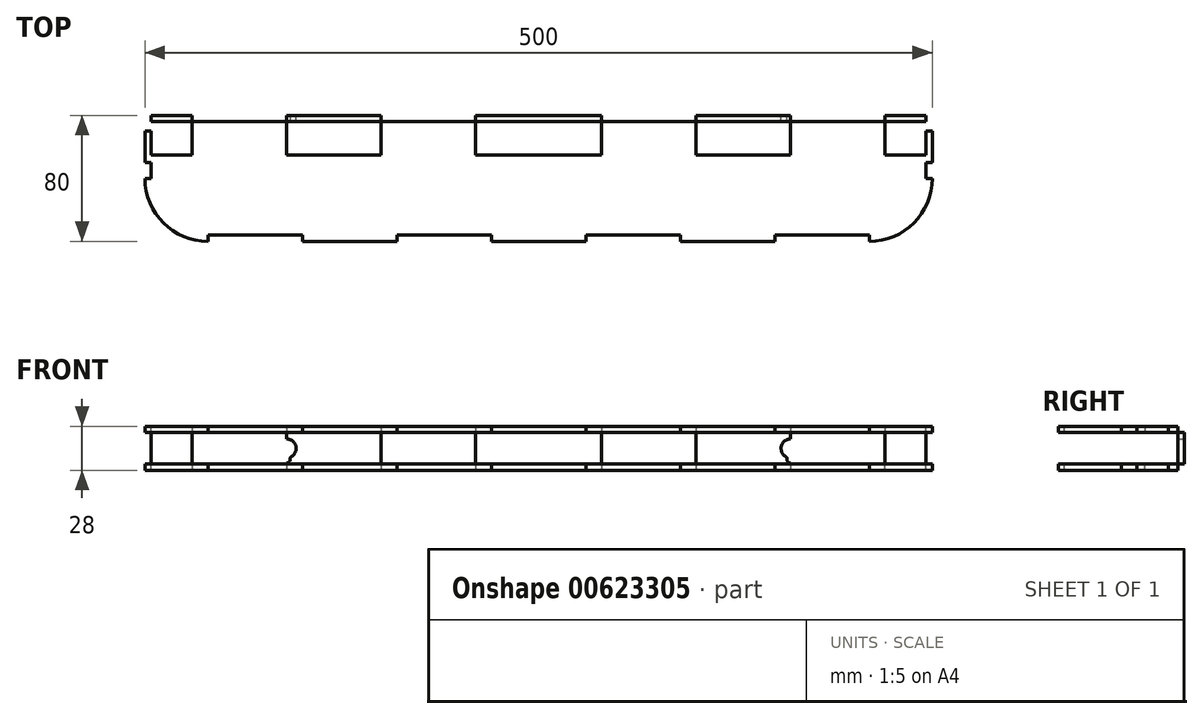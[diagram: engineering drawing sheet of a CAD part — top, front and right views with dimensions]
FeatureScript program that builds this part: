
annotation { "Feature Type Name" : "Feature", "Feature Type Description" : "" }
export const myFeature = defineFeature(function(context is Context, id is Id, definition is map)
    precondition{}
    {
        {
            var Q0;
            Q0=qCreatedBy(makeId("Top.planeOp"),FACE);
            var sketch = newSketch(context, id + "F0", { "sketchPlane" : qUnion([Q0])});
            skLineSegment(sketch, "E0.bottom", {"start": v(-250, 40) * mm, "end": v(250, 40) * mm});
            skLineSegment(sketch, "E0.top", {"start": v(-250, -40) * mm, "end": v(250, -40) * mm});
            skLineSegment(sketch, "E0.left", {"start": v(-250, 40) * mm, "end": v(-250, -40) * mm});
            skLineSegment(sketch, "E0.right", {"start": v(250, 40) * mm, "end": v(250, -40) * mm});
            skPoint(sketch, "E0.middle", {"position": v(0, 0) * mm});
            skSolve(sketch);
        }
        {
            var Q0;
            Q0=makeQuery(id+"F0.imprint","IMPRINT",FACE,{"disambiguationData":[TD([[makeQuery(id+"F0.imprint","IMPRINT",EDGE,{"derivedFrom":sQuery(id+"F0.wireOp",EDGE,"E0.bottom")}),-1.0]])]});
            extrude(context, id + "F1", {"entities" : qUnion([Q0]), "depth" : 4 * mm, "offsetDistance" : 25 * mm});
        }
        {
            var Q0;
            Q0=makeQuery(id+"F1.opExtrude","SWEPT_EDGE",EDGE,{"disambiguationData":[OSD([sQuery(id+"F0.wireOp",EDGE,"E0.top"),sQuery(id+"F0.wireOp",EDGE,"E0.left")])]});
            var Q1;
            Q1=makeQuery(id+"F1.opExtrude","SWEPT_EDGE",EDGE,{"disambiguationData":[OSD([sQuery(id+"F0.wireOp",EDGE,"E0.top"),sQuery(id+"F0.wireOp",EDGE,"E0.right")])]});
            fillet(context, id + "F2", {"entities" : qUnion([Q0, Q1]), "radius" : 40 * mm, "tangentPropagation" : true, "allowEdgeOverflow" : false});
        }
        {
            var Q0;
            Q0=makeQuery(id+"F1.opExtrude","CAP_FACE",FACE,{"disambiguationData":[OSD([sQuery(id+"F0.wireOp",EDGE,"E0.bottom"),sQuery(id+"F0.wireOp",EDGE,"E0.top"),sQuery(id+"F0.wireOp",EDGE,"E0.left"),sQuery(id+"F0.wireOp",EDGE,"E0.right")])],"isStart":true});
            cPlane(context, id + "F3", {"entities" : qUnion([Q0]), "cplaneType" : CPlaneType.OFFSET, "offset" : 10 * mm, "width" : 150 * mm, "height" : 150 * mm});
        }
        {
            var Q0;
            Q0=makeQuery(id+"F1.opExtrude","SWEPT_BODY",BODY,{"disambiguationData":[OSD([sQuery(id+"F0.wireOp",EDGE,"E0.bottom"),sQuery(id+"F0.wireOp",EDGE,"E0.top"),sQuery(id+"F0.wireOp",EDGE,"E0.left"),sQuery(id+"F0.wireOp",EDGE,"E0.right")])]});
            var Q1;
            Q1=qCreatedBy(id+"F3.planeOp",FACE);
            mirror(context, id + "F4", {"entities" : qUnion([Q0]), "mirrorPlane" : qUnion([Q1])});
        }
        {
            var Q0;
            Q0=makeQuery(id+"F1.opExtrude","SWEPT_FACE",FACE,{"disambiguationData":[OSD([sQuery(id+"F0.wireOp",EDGE,"E0.bottom")])]});
            var sketch = newSketch(context, id + "F5", { "sketchPlane" : qUnion([Q0])});
            skLineSegment(sketch, "E1.bottom", {"start": v(-250, 4) * mm, "end": v(250, 4) * mm});
            skLineSegment(sketch, "E1.top", {"start": v(-250, -24) * mm, "end": v(250, -24) * mm});
            skLineSegment(sketch, "E1.left", {"start": v(-250, 4) * mm, "end": v(-250, -24) * mm});
            skLineSegment(sketch, "E1.right", {"start": v(250, 4) * mm, "end": v(250, -24) * mm});
            skSolve(sketch);
        }
        {
            var Q0;
            Q0 = qSketchRegion(id + "F5", true);
            extrude(context, id + "F6", {"entities" : qUnion([Q0]), "oppositeDirection" : true, "depth" : 4 * mm, "offsetDistance" : 25 * mm});
        }
        {
            var Q0;
            Q0=makeQuery(id+"F1.opExtrude","CAP_FACE",FACE,{"disambiguationData":[OSD([sQuery(id+"F0.wireOp",EDGE,"E0.bottom"),sQuery(id+"F0.wireOp",EDGE,"E0.top"),sQuery(id+"F0.wireOp",EDGE,"E0.left"),sQuery(id+"F0.wireOp",EDGE,"E0.right")])],"isStart":false});
            var sketch = newSketch(context, id + "F7", { "sketchPlane" : qUnion([Q0])});
            skLineSegment(sketch, "E2.bottom", {"start": v(-210, -40) * mm, "end": v(-150, -40) * mm});
            skLineSegment(sketch, "E2.top", {"start": v(-210, -36) * mm, "end": v(-150, -36) * mm});
            skLineSegment(sketch, "E2.left", {"start": v(-210, -40) * mm, "end": v(-210, -36) * mm});
            skLineSegment(sketch, "E2.right", {"start": v(-150, -40) * mm, "end": v(-150, -36) * mm});
            skLineSegment(sketch, "E3.bottom", {"start": v(-90, -40) * mm, "end": v(-30, -40) * mm});
            skLineSegment(sketch, "E3.top", {"start": v(-90, -36) * mm, "end": v(-30, -36) * mm});
            skLineSegment(sketch, "E3.left", {"start": v(-90, -40) * mm, "end": v(-90, -36) * mm});
            skLineSegment(sketch, "E3.right", {"start": v(-30, -40) * mm, "end": v(-30, -36) * mm});
            skLineSegment(sketch, "E4.bottom", {"start": v(30, -40) * mm, "end": v(90, -40) * mm});
            skLineSegment(sketch, "E4.top", {"start": v(30, -36) * mm, "end": v(90, -36) * mm});
            skLineSegment(sketch, "E4.left", {"start": v(30, -40) * mm, "end": v(30, -36) * mm});
            skLineSegment(sketch, "E4.right", {"start": v(90, -40) * mm, "end": v(90, -36) * mm});
            skLineSegment(sketch, "E5.bottom", {"start": v(150, -40) * mm, "end": v(210, -40) * mm});
            skLineSegment(sketch, "E5.top", {"start": v(150, -36) * mm, "end": v(210, -36) * mm});
            skLineSegment(sketch, "E5.left", {"start": v(150, -40) * mm, "end": v(150, -36) * mm});
            skLineSegment(sketch, "E5.right", {"start": v(210, -40) * mm, "end": v(210, -36) * mm});
            skLineSegment(sketch, "E6.bottom", {"start": v(-250, 40) * mm, "end": v(-246, 40) * mm});
            skLineSegment(sketch, "E6.top", {"start": v(-250, 30) * mm, "end": v(-246, 30) * mm});
            skLineSegment(sketch, "E6.left", {"start": v(-250, 40) * mm, "end": v(-250, 30) * mm});
            skLineSegment(sketch, "E6.right", {"start": v(-246, 40) * mm, "end": v(-246, 30) * mm});
            skLineSegment(sketch, "E7.bottom", {"start": v(-250, 0) * mm, "end": v(-246, 0) * mm});
            skLineSegment(sketch, "E7.top", {"start": v(-250, 10) * mm, "end": v(-246, 10) * mm});
            skLineSegment(sketch, "E7.left", {"start": v(-250, 0) * mm, "end": v(-250, 10) * mm});
            skLineSegment(sketch, "E7.right", {"start": v(-246, 0) * mm, "end": v(-246, 10) * mm});
            skLineSegment(sketch, "E8.MirrorCS", {"start": v(250, 30) * mm, "end": v(246, 30) * mm});
            skLineSegment(sketch, "E9.MirrorCS", {"start": v(250, 10) * mm, "end": v(246, 10) * mm});
            skLineSegment(sketch, "E10.MirrorCS", {"start": v(250, 0) * mm, "end": v(246, 0) * mm});
            skLineSegment(sketch, "E11.MirrorCS", {"start": v(250, 40) * mm, "end": v(246, 40) * mm});
            skLineSegment(sketch, "E12.MirrorCS", {"start": v(250, 40) * mm, "end": v(250, 30) * mm});
            skLineSegment(sketch, "E13.MirrorCS", {"start": v(250, 0) * mm, "end": v(250, 10) * mm});
            skLineSegment(sketch, "E14.MirrorCS", {"start": v(246, 0) * mm, "end": v(246, 10) * mm});
            skLineSegment(sketch, "E15.MirrorCS", {"start": v(246, 40) * mm, "end": v(246, 30) * mm});
            skSolve(sketch);
        }
        {
            var Q0;
            Q0 = qSketchRegion(id + "F7", true);
            extrude(context, id + "F8", {"entities" : qUnion([Q0]), "operationType" : NewBodyOperationType.REMOVE, "oppositeDirection" : true, "depth" : 61 * mm, "offsetDistance" : 25 * mm});
        }
        {
            var Q0;
            Q0=makeQuery(id+"F6.opExtrude","CAP_FACE",FACE,{"disambiguationData":[OSD([sQuery(id+"F5.wireOp",EDGE,"E1.bottom"),sQuery(id+"F5.wireOp",EDGE,"E1.top"),sQuery(id+"F5.wireOp",EDGE,"E1.left"),sQuery(id+"F5.wireOp",EDGE,"E1.right")])],"isStart":true});
            var sketch = newSketch(context, id + "F9", { "sketchPlane" : qUnion([Q0])});
            skLineSegment(sketch, "E16.bottom", {"start": v(-246, 0) * mm, "end": v(246, 0) * mm});
            skLineSegment(sketch, "E16.top", {"start": v(-246, 4) * mm, "end": v(246, 4) * mm});
            skLineSegment(sketch, "E16.left", {"start": v(-246, 0) * mm, "end": v(-246, 4) * mm});
            skLineSegment(sketch, "E16.right", {"start": v(246, 0) * mm, "end": v(246, 4) * mm});
            skLineSegment(sketch, "E17.bottom", {"start": v(-246, -24) * mm, "end": v(246, -24) * mm});
            skLineSegment(sketch, "E17.top", {"start": v(-246, -20) * mm, "end": v(246, -20) * mm});
            skLineSegment(sketch, "E17.left", {"start": v(-246, -24) * mm, "end": v(-246, -20) * mm});
            skLineSegment(sketch, "E17.right", {"start": v(246, -24) * mm, "end": v(246, -20) * mm});
            skSolve(sketch);
        }
        {
            var Q0;
            Q0 = qSketchRegion(id + "F9", true);
            extrude(context, id + "F10", {"entities" : qUnion([Q0]), "operationType" : NewBodyOperationType.REMOVE, "oppositeDirection" : true, "depth" : 4 * mm, "offsetDistance" : 25 * mm});
        }
        {
            var Q0;
            Q0=makeQuery(id+"F4.opPattern","COPY",FACE,{"derivedFrom":makeQuery(id+"F1.opExtrude","CAP_FACE",FACE,{"disambiguationData":[OSD([sQuery(id+"F0.wireOp",EDGE,"E0.bottom"),sQuery(id+"F0.wireOp",EDGE,"E0.top"),sQuery(id+"F0.wireOp",EDGE,"E0.left"),sQuery(id+"F0.wireOp",EDGE,"E0.right")])],"isStart":false}),"instanceName":"1"});
            var sketch = newSketch(context, id + "F11", { "sketchPlane" : qUnion([Q0])});
            skLineSegment(sketch, "E18.bottom", {"start": v(-220, -36) * mm, "end": v(-160, -36) * mm});
            skLineSegment(sketch, "E18.top", {"start": v(-220, -40) * mm, "end": v(-160, -40) * mm});
            skLineSegment(sketch, "E18.left", {"start": v(-220, -36) * mm, "end": v(-220, -40) * mm});
            skLineSegment(sketch, "E18.right", {"start": v(-160, -36) * mm, "end": v(-160, -40) * mm});
            skLineSegment(sketch, "E19.bottom", {"start": v(-100, -36) * mm, "end": v(-40, -36) * mm});
            skLineSegment(sketch, "E19.top", {"start": v(-100, -40) * mm, "end": v(-40, -40) * mm});
            skLineSegment(sketch, "E19.left", {"start": v(-100, -36) * mm, "end": v(-100, -40) * mm});
            skLineSegment(sketch, "E19.right", {"start": v(-40, -36) * mm, "end": v(-40, -40) * mm});
            skLineSegment(sketch, "E20.MirrorCS", {"start": v(40, -36) * mm, "end": v(40, -40) * mm});
            skLineSegment(sketch, "E21.MirrorCS", {"start": v(100, -36) * mm, "end": v(100, -40) * mm});
            skLineSegment(sketch, "E22.MirrorCS", {"start": v(220, -36) * mm, "end": v(220, -40) * mm});
            skLineSegment(sketch, "E23.MirrorCS", {"start": v(160, -36) * mm, "end": v(160, -40) * mm});
            skLineSegment(sketch, "E24.MirrorCS", {"start": v(100, -40) * mm, "end": v(40, -40) * mm});
            skLineSegment(sketch, "E25.MirrorCS", {"start": v(100, -36) * mm, "end": v(40, -36) * mm});
            skLineSegment(sketch, "E26.MirrorCS", {"start": v(220, -36) * mm, "end": v(160, -36) * mm});
            skLineSegment(sketch, "E27.MirrorCS", {"start": v(220, -40) * mm, "end": v(160, -40) * mm});
            skSolve(sketch);
        }
        {
            var Q0;
            {var subQ14=sQuery(id+"F11.wireOp",EDGE,"E18.bottom");Q0=makeQuery(id+"F11.imprint","IMPRINT",FACE,{"disambiguationData":[TD([[makeQuery(id+"F11.imprint","IMPRINT",EDGE,{"derivedFrom":subQ14}),-1.0]])]});}
            var sketch = newSketch(context, id + "F12", { "sketchPlane" : qUnion([Q0])});
            skLineSegment(sketch, "E28.bottom", {"start": v(-246, -36) * mm, "end": v(246, -36) * mm});
            skLineSegment(sketch, "E28.top", {"start": v(-246, -40) * mm, "end": v(246, -40) * mm});
            skLineSegment(sketch, "E28.left", {"start": v(-246, -36) * mm, "end": v(-246, -40) * mm});
            skLineSegment(sketch, "E28.right", {"start": v(246, -36) * mm, "end": v(246, -40) * mm});
            skSolve(sketch);
        }
        {
            var Q0;
            Q0 = qSketchRegion(id + "F12", true);
            extrude(context, id + "F13", {"entities" : qUnion([Q0]), "operationType" : NewBodyOperationType.ADD, "oppositeDirection" : true, "depth" : 4 * mm, "offsetDistance" : 25 * mm});
        }
        {
            var Q0;
            Q0 = qSketchRegion(id + "F11", true);
            extrude(context, id + "F14", {"entities" : qUnion([Q0]), "operationType" : NewBodyOperationType.REMOVE, "oppositeDirection" : true, "depth" : 25 * mm, "offsetDistance" : 25 * mm});
        }
        {
            var Q0;
            Q0=makeQuery(id+"F6.opExtrude","CAP_FACE",FACE,{"disambiguationData":[OSD([sQuery(id+"F5.wireOp",EDGE,"E1.bottom"),sQuery(id+"F5.wireOp",EDGE,"E1.top"),sQuery(id+"F5.wireOp",EDGE,"E1.left"),sQuery(id+"F5.wireOp",EDGE,"E1.right")])],"isStart":true});
            var sketch = newSketch(context, id + "F15", { "sketchPlane" : qUnion([Q0])});
            skLineSegment(sketch, "E29.bottom", {"start": v(220, -24) * mm, "end": v(246, -24) * mm});
            skLineSegment(sketch, "E29.top", {"start": v(220, -20) * mm, "end": v(246, -20) * mm});
            skLineSegment(sketch, "E29.left", {"start": v(220, -24) * mm, "end": v(220, -20) * mm});
            skLineSegment(sketch, "E29.right", {"start": v(246, -24) * mm, "end": v(246, -20) * mm});
            skLineSegment(sketch, "E30.bottom", {"start": v(160, -24) * mm, "end": v(100, -24) * mm});
            skLineSegment(sketch, "E30.top", {"start": v(160, -20) * mm, "end": v(100, -20) * mm});
            skLineSegment(sketch, "E30.left", {"start": v(160, -24) * mm, "end": v(160, -20) * mm});
            skLineSegment(sketch, "E30.right", {"start": v(100, -24) * mm, "end": v(100, -20) * mm});
            skLineSegment(sketch, "E31.bottom", {"start": v(40, -24) * mm, "end": v(-40, -24) * mm});
            skLineSegment(sketch, "E31.top", {"start": v(40, -20) * mm, "end": v(-40, -20) * mm});
            skLineSegment(sketch, "E31.left", {"start": v(40, -24) * mm, "end": v(40, -20) * mm});
            skLineSegment(sketch, "E31.right", {"start": v(-40, -24) * mm, "end": v(-40, -20) * mm});
            skLineSegment(sketch, "E32.MirrorCS", {"start": v(-246, -24) * mm, "end": v(-246, -20) * mm});
            skLineSegment(sketch, "E33.MirrorCS", {"start": v(-220, -24) * mm, "end": v(-220, -20) * mm});
            skLineSegment(sketch, "E34.MirrorCS", {"start": v(-100, -24) * mm, "end": v(-100, -20) * mm});
            skLineSegment(sketch, "E35.MirrorCS", {"start": v(-160, -24) * mm, "end": v(-160, -20) * mm});
            skLineSegment(sketch, "E36.MirrorCS", {"start": v(-220, -24) * mm, "end": v(-246, -24) * mm});
            skLineSegment(sketch, "E37.MirrorCS", {"start": v(-220, -20) * mm, "end": v(-246, -20) * mm});
            skLineSegment(sketch, "E38.MirrorCS", {"start": v(-160, -20) * mm, "end": v(-100, -20) * mm});
            skLineSegment(sketch, "E39.MirrorCS", {"start": v(-160, -24) * mm, "end": v(-100, -24) * mm});
            skLineSegment(sketch, "E40", {"start": v(0, -10) * mm, "end": v(11.23, -10) * mm, "construction": true});
            skLineSegment(sketch, "E41.MirrorCS", {"start": v(40, 4) * mm, "end": v(40, 0) * mm});
            skLineSegment(sketch, "E42.MirrorCS", {"start": v(-40, 4) * mm, "end": v(-40, 0) * mm});
            skLineSegment(sketch, "E43.MirrorCS", {"start": v(160, 4) * mm, "end": v(160, 0) * mm});
            skLineSegment(sketch, "E44.MirrorCS", {"start": v(246, 4) * mm, "end": v(246, 0) * mm});
            skLineSegment(sketch, "E45.MirrorCS", {"start": v(220, 4) * mm, "end": v(220, 0) * mm});
            skLineSegment(sketch, "E46.MirrorCS", {"start": v(100, 4) * mm, "end": v(100, 0) * mm});
            skLineSegment(sketch, "E47.MirrorCS", {"start": v(-246, 4) * mm, "end": v(-246, 0) * mm});
            skLineSegment(sketch, "E48.MirrorCS", {"start": v(-100, 4) * mm, "end": v(-100, 0) * mm});
            skLineSegment(sketch, "E49.MirrorCS", {"start": v(-220, 4) * mm, "end": v(-220, 0) * mm});
            skLineSegment(sketch, "E50.MirrorCS", {"start": v(-160, 4) * mm, "end": v(-160, 0) * mm});
            skLineSegment(sketch, "E51.MirrorCS", {"start": v(-160, 4) * mm, "end": v(-100, 4) * mm});
            skLineSegment(sketch, "E52.MirrorCS", {"start": v(40, 0) * mm, "end": v(-40, 0) * mm});
            skLineSegment(sketch, "E53.MirrorCS", {"start": v(220, 4) * mm, "end": v(246, 4) * mm});
            skLineSegment(sketch, "E54.MirrorCS", {"start": v(-220, 4) * mm, "end": v(-246, 4) * mm});
            skLineSegment(sketch, "E55.MirrorCS", {"start": v(-220, 0) * mm, "end": v(-246, 0) * mm});
            skLineSegment(sketch, "E56.MirrorCS", {"start": v(160, 0) * mm, "end": v(100, 0) * mm});
            skLineSegment(sketch, "E57.MirrorCS", {"start": v(40, 4) * mm, "end": v(-40, 4) * mm});
            skLineSegment(sketch, "E58.MirrorCS", {"start": v(-160, 0) * mm, "end": v(-100, 0) * mm});
            skLineSegment(sketch, "E59.MirrorCS", {"start": v(220, 0) * mm, "end": v(246, 0) * mm});
            skLineSegment(sketch, "E60.MirrorCS", {"start": v(160, 4) * mm, "end": v(100, 4) * mm});
            skSolve(sketch);
        }
        {
            var Q0;
            Q0 = qSketchRegion(id + "F15", true);
            extrude(context, id + "F16", {"entities" : qUnion([Q0]), "operationType" : NewBodyOperationType.REMOVE, "oppositeDirection" : true, "depth" : 25 * mm, "offsetDistance" : 25 * mm});
        }
        {
            var Q0;
            Q0=makeQuery(id+"F6.opExtrude","CAP_FACE",FACE,{"disambiguationData":[OSD([sQuery(id+"F5.wireOp",EDGE,"E1.bottom"),sQuery(id+"F5.wireOp",EDGE,"E1.top"),sQuery(id+"F5.wireOp",EDGE,"E1.left"),sQuery(id+"F5.wireOp",EDGE,"E1.right")])],"isStart":true});
            var sketch = newSketch(context, id + "F17", { "sketchPlane" : qUnion([Q0])});
            skArc(sketch, "E61", {"start": v(-157.75, -15.56) * mm, "mid": v(-160, -4) * mm, "end": v(-162.25, -15.56) * mm});
            skArc(sketch, "E62", {"start": v(-162.25, -17) * mm, "mid": v(-160, -19.25) * mm, "end": v(-157.75, -17) * mm});
            skLineSegment(sketch, "E63", {"start": v(-162.25, -17) * mm, "end": v(-162.25, -15.56) * mm});
            skLineSegment(sketch, "E64", {"start": v(-157.75, -17) * mm, "end": v(-157.75, -15.56) * mm});
            skLineSegment(sketch, "E65.MirrorCS", {"start": v(157.75, -17) * mm, "end": v(157.75, -15.56) * mm});
            skLineSegment(sketch, "E66.MirrorCS", {"start": v(162.25, -17) * mm, "end": v(162.25, -15.56) * mm});
            skArc(sketch, "E67.MirrorCS", {"start": v(162.25, -17) * mm, "mid": v(160, -19.25) * mm, "end": v(157.75, -17) * mm});
            skArc(sketch, "E68.MirrorCS", {"start": v(157.75, -15.56) * mm, "mid": v(160, -4) * mm, "end": v(162.25, -15.56) * mm});
            skSolve(sketch);
        }
        {
            var Q0;
            Q0 = qSketchRegion(id + "F17", true);
            extrude(context, id + "F18", {"entities" : qUnion([Q0]), "operationType" : NewBodyOperationType.REMOVE, "oppositeDirection" : true, "depth" : 25 * mm, "offsetDistance" : 25 * mm});
        }
        {
            var Q0;
            Q0=makeQuery(id+"F18.boolean.opBoolean","COPY",EDGE,{"derivedFrom":makeQuery(id+"F18.opExtrude","SWEPT_EDGE",EDGE,{"disambiguationData":[OSD([sQuery(id+"F17.wireOp",EDGE,"E61"),sQuery(id+"F17.wireOp",EDGE,"E63")])]})});
            var Q1;
            Q1=makeQuery(id+"F18.boolean.opBoolean","COPY",EDGE,{"derivedFrom":makeQuery(id+"F18.opExtrude","SWEPT_EDGE",EDGE,{"disambiguationData":[OSD([sQuery(id+"F17.wireOp",EDGE,"E61"),sQuery(id+"F17.wireOp",EDGE,"E64")])]})});
            var Q2;
            Q2=makeQuery(id+"F18.boolean.opBoolean","COPY",EDGE,{"derivedFrom":makeQuery(id+"F18.opExtrude","SWEPT_EDGE",EDGE,{"disambiguationData":[OSD([sQuery(id+"F17.wireOp",EDGE,"E66.MirrorCS"),sQuery(id+"F17.wireOp",EDGE,"E68.MirrorCS")])]})});
            var Q3;
            Q3=makeQuery(id+"F18.boolean.opBoolean","COPY",EDGE,{"derivedFrom":makeQuery(id+"F18.opExtrude","SWEPT_EDGE",EDGE,{"disambiguationData":[OSD([sQuery(id+"F17.wireOp",EDGE,"E65.MirrorCS"),sQuery(id+"F17.wireOp",EDGE,"E68.MirrorCS")])]})});
            fillet(context, id + "F19", {"entities" : qUnion([Q0, Q1, Q2, Q3]), "radius" : 1 * mm, "tangentPropagation" : true, "allowEdgeOverflow" : false});
        }
    });
